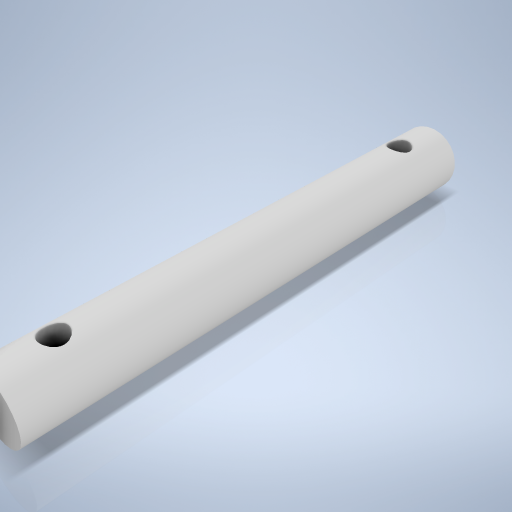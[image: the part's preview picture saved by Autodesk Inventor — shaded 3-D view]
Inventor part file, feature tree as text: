
AUTODESK INVENTOR PART (.ipt)
format: ipt  version: 2024.2 (Build 282272000, 272)  size: 252,416 bytes
history: native  units: mm
features: sketch x2, extrude x1, plane x1, hole x1
ambient origin geometry x8: Origin, YZ Plane, XZ Plane, XY Plane, X Axis, Y Axis, Z Axis, Center Point
bodies: Volumenkörper1 (feature_tree)
feature tree (5):
  extrude  "Extrusion1"  Depth=120.0mm TaperAngle=0.0deg
  plane  "Arbeitsebene1"
  hole  "Bohrung1"  [1 undecoded]
  sketch  "Skizze1"  dims[d0=16.0mm d1=120.0mm d2=0.0mm]
  sketch  "Skizze2"  dims[d3=8.0mm d6=6.0mm d7=6.0mm d8=4.0mm d9=2.0mm d10=90.0deg d11=8.0mm d12=20.594885mm d13=94.5mm d14=120.0mm]
note: 1 required parameter value undecoded (feature->parameter linkage not recoverable at this tier; creation-order binding heuristic only, values carry confidence <= 0.55)
